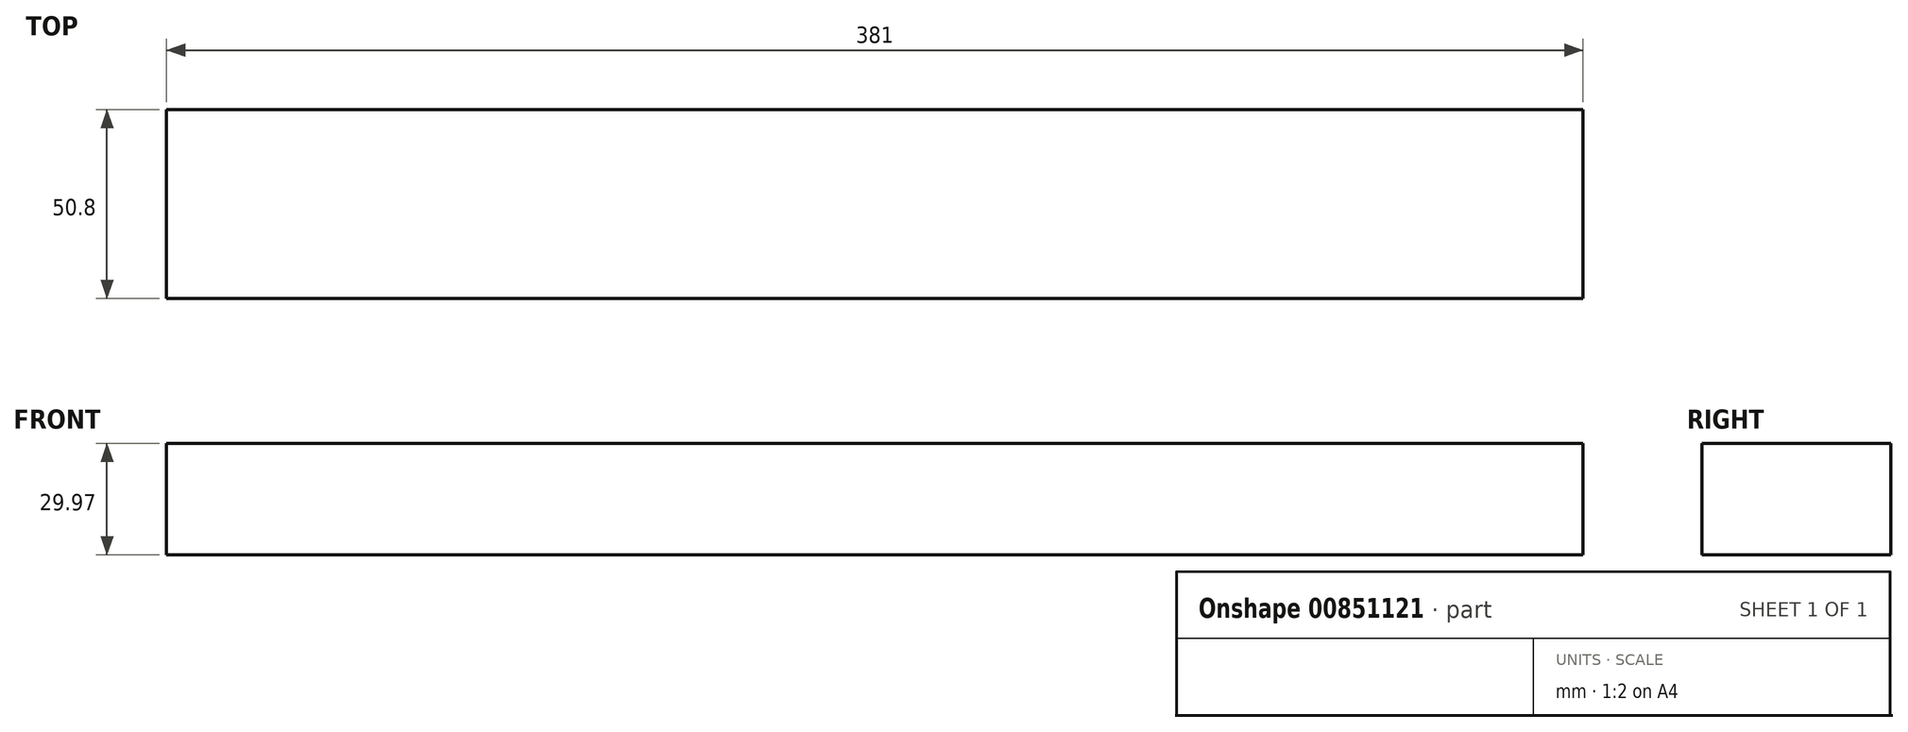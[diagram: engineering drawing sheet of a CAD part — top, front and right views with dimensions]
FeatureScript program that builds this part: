
annotation { "Feature Type Name" : "Feature", "Feature Type Description" : "" }
export const myFeature = defineFeature(function(context is Context, id is Id, definition is map)
    precondition{}
    {
        {
            var Q0;
            Q0=qCreatedBy(makeId("Top.planeOp"),FACE);
            var sketch = newSketch(context, id + "F0", { "sketchPlane" : qUnion([Q0])});
            skLineSegment(sketch, "E0.bottom", {"start": v(-191.13, 29.13) * mm, "end": v(189.87, 29.13) * mm});
            skLineSegment(sketch, "E0.top", {"start": v(-191.13, -21.67) * mm, "end": v(189.87, -21.67) * mm});
            skLineSegment(sketch, "E0.left", {"start": v(-191.13, 29.13) * mm, "end": v(-191.13, -21.67) * mm});
            skLineSegment(sketch, "E0.right", {"start": v(189.87, 29.13) * mm, "end": v(189.87, -21.67) * mm});
            skSolve(sketch);
        }
        {
            var Q0;
            Q0=makeQuery(id+"F0.imprint","IMPRINT",FACE,{"disambiguationData":[TD([[makeQuery(id+"F0.imprint","IMPRINT",EDGE,{"derivedFrom":sQuery(id+"F0.wireOp",EDGE,"E0.bottom")}),-1.0]])]});
            extrude(context, id + "F1", {"entities" : qUnion([Q0]), "depth" : 29.97 * mm, "offsetDistance" : 25.4 * mm});
        }
    });
